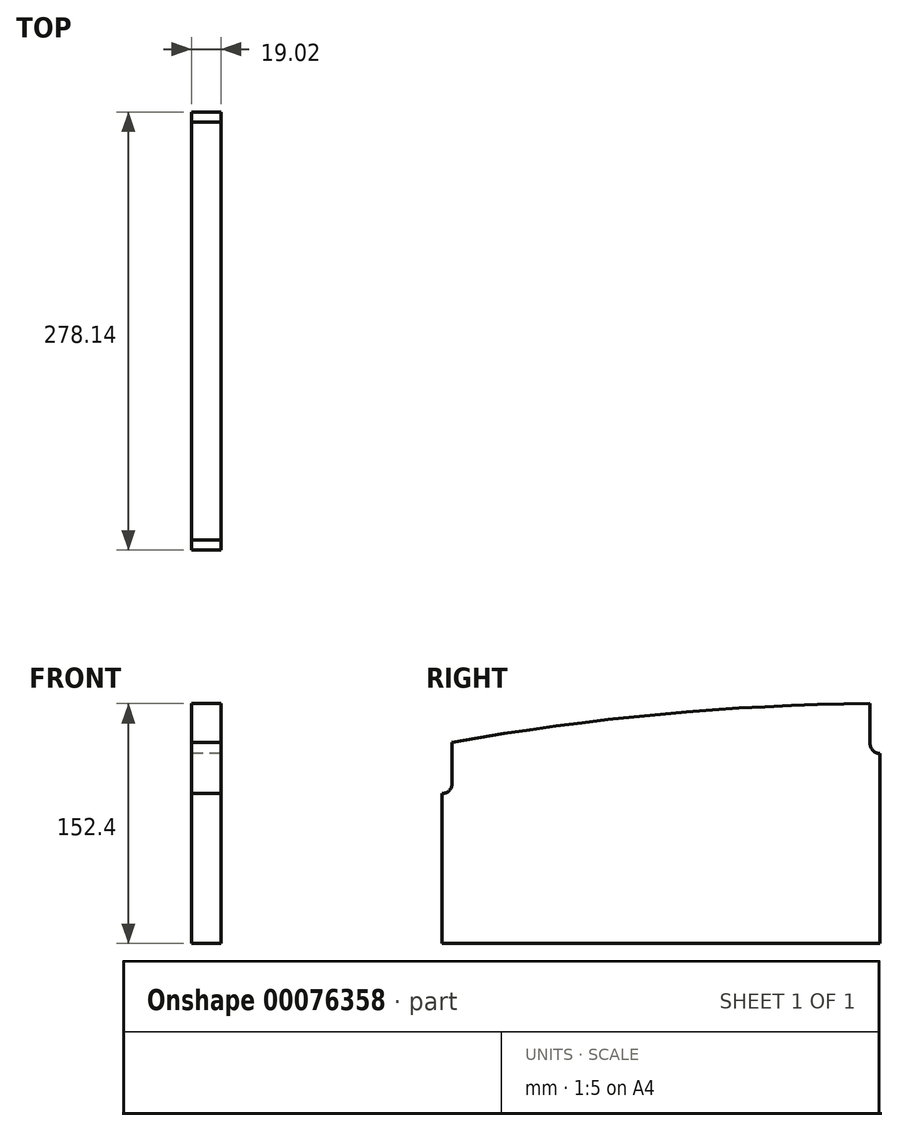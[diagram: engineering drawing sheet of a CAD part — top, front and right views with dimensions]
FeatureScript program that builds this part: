
annotation { "Feature Type Name" : "Feature", "Feature Type Description" : "" }
export const myFeature = defineFeature(function(context is Context, id is Id, definition is map)
    precondition{}
    {
        {
            var Q0;
            Q0=qCreatedBy(makeId("Right.planeOp"),FACE);
            var sketch = newSketch(context, id + "F0", { "sketchPlane" : qUnion([Q0])});
            skLineSegment(sketch, "E0.rect.bottom", {"start": v(136.46, -76.2) * mm, "end": v(-141.68, -76.2) * mm});
            skLineSegment(sketch, "E0.rect.left", {"start": v(136.46, -76.2) * mm, "end": v(136.46, 44.45) * mm});
            skLineSegment(sketch, "E0.rect.right", {"start": v(-141.68, -76.2) * mm, "end": v(-141.68, 19.05) * mm});
            skPoint(sketch, "E0.rect.middle", {"position": v(0, 0) * mm});
            skLineSegment(sketch, "E1.bottom", {"start": v(-141.68, 19.05) * mm, "end": v(-141.68, 19.05) * mm});
            skLineSegment(sketch, "E1.right", {"start": v(-135.33, 25.4) * mm, "end": v(-135.33, 51.6) * mm});
            skPoint(sketch, "E2.visualSharp", {"position": v(-135.33, 19.05) * mm});
            skArc(sketch, "E2.filletArc", {"start": v(-141.68, 19.05) * mm, "mid": v(-137.2, 20.9) * mm, "end": v(-135.33, 25.4) * mm});
            skLineSegment(sketch, "E3.bottom", {"start": v(136.46, 44.45) * mm, "end": v(136.46, 44.45) * mm});
            skLineSegment(sketch, "E3.right", {"start": v(130.11, 50.8) * mm, "end": v(130.11, 76.2) * mm});
            skPoint(sketch, "E4.visualSharp", {"position": v(130.11, 44.45) * mm});
            skArc(sketch, "E4.filletArc", {"start": v(130.11, 50.8) * mm, "mid": v(131.97, 46.3) * mm, "end": v(136.46, 44.45) * mm});
            skArc(sketch, "E5", {"start": v(130.11, 76.2) * mm, "mid": v(-3.12, 69.38) * mm, "end": v(-135.33, 51.6) * mm});
            skSolve(sketch);
        }
        {
            var Q0;
            Q0=makeQuery(id+"F0.imprint","IMPRINT",FACE,{"disambiguationData":[TD([[makeQuery(id+"F0.imprint","IMPRINT",EDGE,{"derivedFrom":sQuery(id+"F0.wireOp",EDGE,"E0.rect.bottom")}),-1.0]])]});
            extrude(context, id + "F1", {"entities" : qUnion([Q0]), "depth" : 19.02 * mm});
        }
    });
